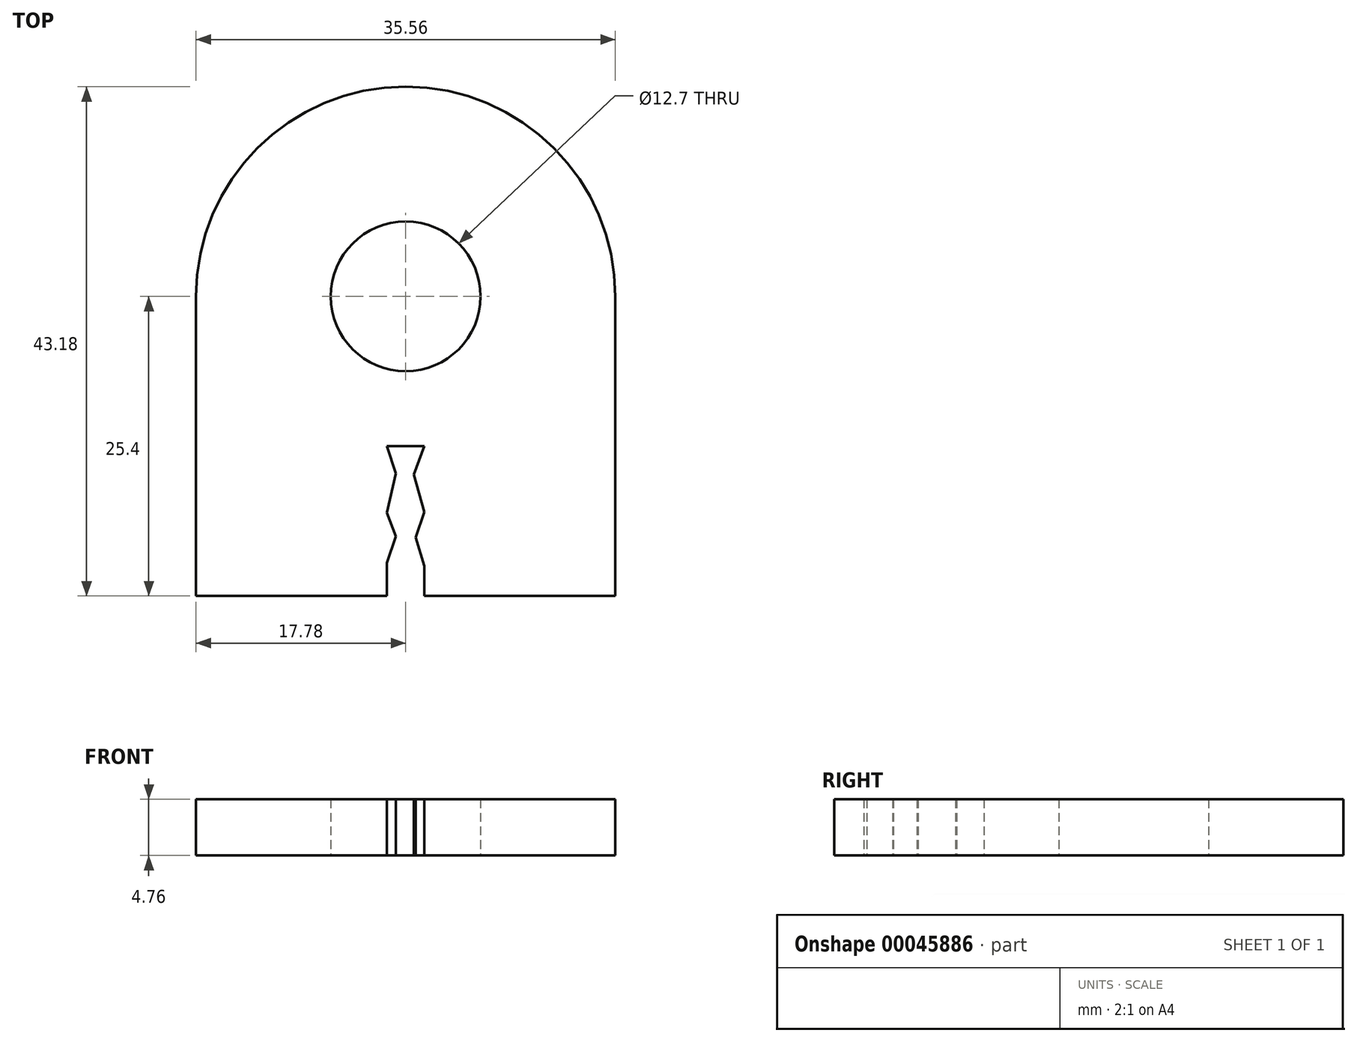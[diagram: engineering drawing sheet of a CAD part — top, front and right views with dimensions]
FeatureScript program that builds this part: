
annotation { "Feature Type Name" : "Feature", "Feature Type Description" : "" }
export const myFeature = defineFeature(function(context is Context, id is Id, definition is map)
    precondition{}
    {
        {
            var Q0;
            Q0=qCreatedBy(makeId("Top.planeOp"),FACE);
            var sketch = newSketch(context, id + "F0", { "sketchPlane" : qUnion([Q0])});
            skArc(sketch, "E0", {"start": v(17.78, 0) * mm, "mid": v(0, 17.78) * mm, "end": v(-17.78, 0) * mm});
            skCircle(sketch, "E1", {"center": v(0, 0) * mm, "radius": 6.35 * mm});
            skLineSegment(sketch, "E2", {"start": v(-17.78, 0) * mm, "end": v(-17.78, -25.4) * mm});
            skLineSegment(sketch, "E3", {"start": v(17.78, 0) * mm, "end": v(17.78, -25.4) * mm});
            skLineSegment(sketch, "E4", {"start": v(-17.78, -25.4) * mm, "end": v(17.78, -25.4) * mm});
            skLineSegment(sketch, "E5", {"start": v(-1.59, -22.62) * mm, "end": v(-1.59, -25.4) * mm});
            skPoint(sketch, "E6.orphan", {"position": v(-1.59, 0) * mm});
            skPoint(sketch, "E7.orphan", {"position": v(1.59, 0) * mm});
            skLineSegment(sketch, "E8", {"start": v(1.59, -12.7) * mm, "end": v(-1.59, -12.7) * mm});
            skLineSegment(sketch, "E9", {"start": v(-1.59, -12.7) * mm, "end": v(-0.83, -15) * mm});
            skLineSegment(sketch, "E10", {"start": v(-0.83, -15) * mm, "end": v(-1.59, -18.35) * mm});
            skLineSegment(sketch, "E11", {"start": v(-1.59, -18.35) * mm, "end": v(-0.83, -20.36) * mm});
            skLineSegment(sketch, "E12", {"start": v(-0.83, -20.36) * mm, "end": v(-1.59, -22.62) * mm});
            skLineSegment(sketch, "E13", {"start": v(1.59, -12.7) * mm, "end": v(0.68, -15.1) * mm});
            skLineSegment(sketch, "E14", {"start": v(0.68, -15.1) * mm, "end": v(1.59, -18.27) * mm});
            skLineSegment(sketch, "E15", {"start": v(1.59, -18.27) * mm, "end": v(0.84, -20.44) * mm});
            skLineSegment(sketch, "E16", {"start": v(0.84, -20.44) * mm, "end": v(1.59, -22.87) * mm});
            skLineSegment(sketch, "E17.trimOffspring", {"start": v(1.59, -22.87) * mm, "end": v(1.59, -25.4) * mm});
            skPoint(sketch, "E18.end.orphan", {"position": v(15.39, -12.7) * mm});
            skSolve(sketch);
        }
        {
            var Q0;
            Q0=makeQuery(id+"F0.imprint","IMPRINT",FACE,{"disambiguationData":[TD([[makeQuery(id+"F0.imprint","IMPRINT",EDGE,{"derivedFrom":sQuery(id+"F0.wireOp",EDGE,"E0")}),1.0]])]});
            extrude(context, id + "F1", {"entities" : qUnion([Q0]), "depth" : 4.76 * mm});
        }
    });
